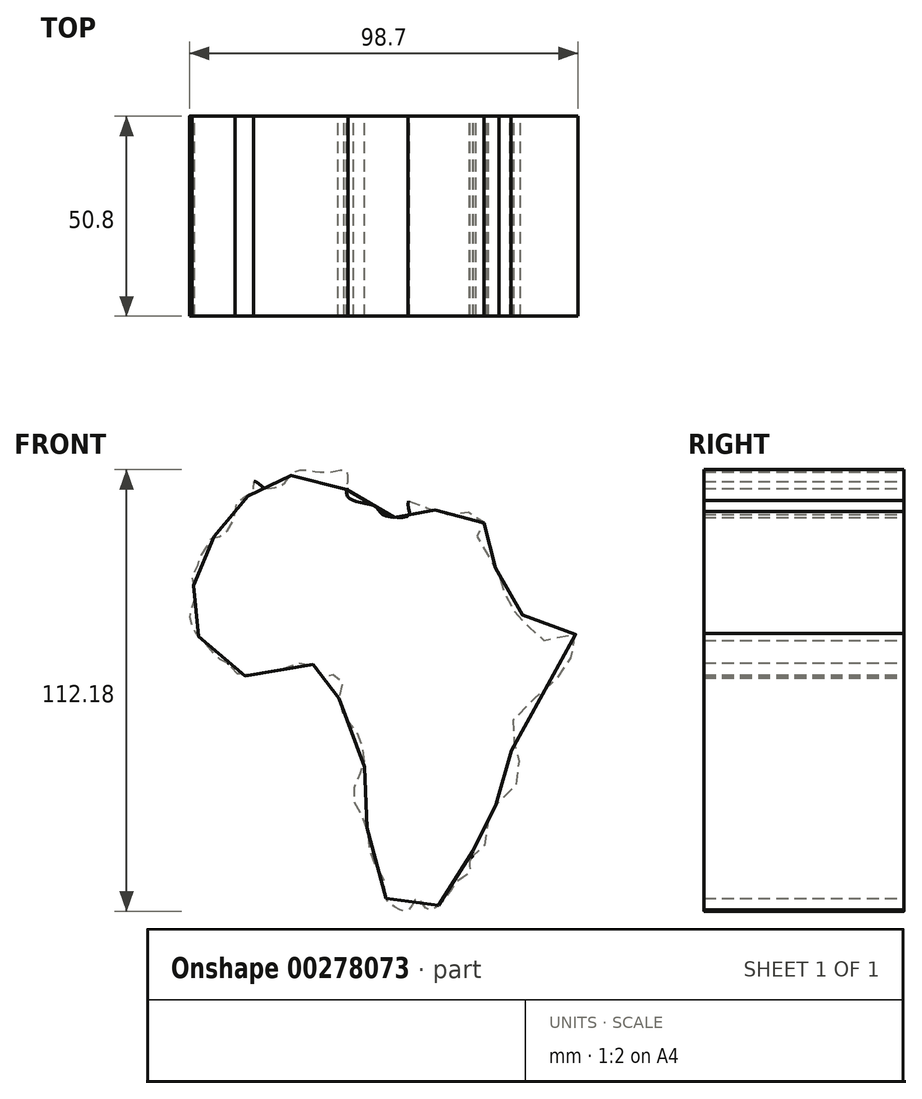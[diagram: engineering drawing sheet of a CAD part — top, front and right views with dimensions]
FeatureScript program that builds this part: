
annotation { "Feature Type Name" : "Feature", "Feature Type Description" : "" }
export const myFeature = defineFeature(function(context is Context, id is Id, definition is map)
    precondition{}
    {
        {
            var Q0;
            Q0=qCreatedBy(makeId("Front.planeOp"),FACE);
            var sketch = newSketch(context, id + "F0", { "sketchPlane" : qUnion([Q0])});
            skPoint(sketch, "E0.91.internal.snap0", {"position": v(-57.95, 3.06) * mm});
            skFitSpline(sketch, "E0", {"points": [v(-5.8, -49.74) * mm, v(-6.44, -44.6) * mm, v(-9.02, -40.4) * mm, v(-9.98, -36.87) * mm, v(-10.3, -33) * mm, v(-12.56, -27.53) * mm, v(-13.84, -25.27) * mm, v(-13.84, -22.06) * mm, v(-12.56, -18.2) * mm, v(-11.27, -16.26) * mm, v(-11.6, -13.04) * mm, v(-11.91, -10.46) * mm, v(-13.84, -6.6) * mm, v(-18.03, 0) * mm, v(-16.42, 3.7) * mm, v(-17.7, 6.28) * mm, v(-19.64, 6.92) * mm, v(-21.57, 6.28) * mm, v(-22.22, 7.57) * mm, v(-24.8, 9.82) * mm, v(-29.3, 9.5) * mm, v(-32.84, 8.21) * mm, v(-35.1, 7.89) * mm, v(-39.6, 6.92) * mm, v(-43.47, 7.24) * mm, v(-45.4, 9.5) * mm, v(-47.65, 10.79) * mm, v(-48.94, 11.75) * mm, v(-51.84, 15.3) * mm, v(-54.41, 17.87) * mm, v(-55.06, 19.8) * mm, v(-55.7, 22.38) * mm, v(-54.74, 24.63) * mm, v(-54.41, 26.88) * mm, v(-54.74, 29.46) * mm, v(-54.74, 30.43) * mm, v(-55.06, 31.4) * mm, v(-53.45, 35.26) * mm, v(-52.48, 37.83) * mm, v(-50.87, 40.4) * mm, v(-49.9, 42.02) * mm, v(-47.33, 42.34) * mm, v(-45.4, 44.92) * mm, v(-44.11, 47.17) * mm, v(-44.11, 49.42) * mm, v(-42.5, 52) * mm, v(-39.6, 53.29) * mm, v(-39.28, 56.18) * mm, v(-36.7, 54.57) * mm, v(-34.45, 54.57) * mm, v(-32.2, 55.22) * mm, v(-28.66, 58.76) * mm, v(-24.15, 58.76) * mm, v(-19, 58.76) * mm, v(-15.78, 58.76) * mm, v(-15.78, 53.29) * mm, v(-14.81, 51.68) * mm, v(-11.91, 50.71) * mm, v(-8.37, 49.74) * mm, v(-7.4, 48.46) * mm, v(-4.83, 47.17) * mm, v(0, 47.5) * mm, v(0, 49.1) * mm, v(0, 51.35) * mm, v(2.25, 50.07) * mm, v(4.83, 49.42) * mm, v(7.73, 48.46) * mm, v(9.98, 47.81) * mm, v(12.23, 48.13) * mm, v(15.13, 48.46) * mm, v(17.7, 48.13) * mm, v(19, 46.2) * mm, v(18.35, 43.63) * mm, v(17.06, 42.98) * mm, v(18.67, 40.73) * mm, v(20.28, 37.83) * mm, v(20.6, 35.26) * mm, v(22.22, 33.97) * mm, v(22.86, 30.75) * mm, v(23.18, 28.5) * mm, v(25.76, 26.56) * mm, v(26.08, 23.66) * mm, v(28.66, 22.38) * mm, v(29.94, 20.12) * mm, v(31.88, 17.55) * mm, v(33.49, 15.94) * mm, v(36.38, 16.26) * mm, v(42.5, 17.23) * mm, v(42.18, 12.72) * mm, v(40.25, 10.46) * mm, v(38, 6.92) * mm, v(35.42, 3.06) * mm, v(30.27, 0) * mm, v(26.72, -4.02) * mm, v(25.76, -7.89) * mm, v(26.72, -9.82) * mm, v(26.08, -12.72) * mm, v(28.01, -14.97) * mm, v(28.01, -18.2) * mm, v(26.72, -22.06) * mm, v(24.15, -24.95) * mm, v(20.28, -26.88) * mm, v(19.96, -29.46) * mm, v(20.28, -33) * mm, v(19.32, -36.22) * mm, v(16.42, -36.87) * mm, v(16.42, -38.48) * mm, v(15.45, -40.4) * mm, v(15.45, -42.98) * mm, v(12.56, -45.24) * mm, v(9.66, -49.1) * mm, v(4.83, -52.64) * mm, v(2.25, -49.74) * mm, v(0, -52.64) * mm, v(-2.25, -52.64) * mm, v(-5.8, -49.74) * mm]});
            skSolve(sketch);
        }
        {
            var Q0;
            Q0 = qSketchRegion(id + "F0", true);
            extrude(context, id + "F1", {"entities" : qUnion([Q0]), "depth" : 50.8 * mm});
        }
    });
